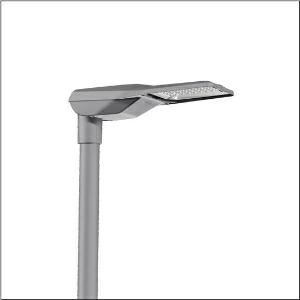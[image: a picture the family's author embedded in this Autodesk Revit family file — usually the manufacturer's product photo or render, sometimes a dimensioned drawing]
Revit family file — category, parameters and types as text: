
# Revit family: streetlight_sl_21_iq_mini___stw1_0a_5xe2e61d08hb_c7c8
name_source: partatom
category: Lighting Fixtures
units: mm (PartAtom-declared; Revit-internal decimal feet)

## family parameters
Cut with Voids When Loaded = No
Host = Face
Light Source = No
Part Type = Normal
Room Calculation Point = No
Round Connector Dimension = Use Diameter
Shared = No

## types (1)
- --- (1 x LED, 8480 lm, 70.9 W, 2700K)
    Apparent Load = 71 VA
    CIE Flux Codes = 38 75 98 100 100
    Color Rendering = 70
    Color Temperature = 2700K
    Default Elevation = 1800 mm
    Description = Streetlight SL 21 iQ mini, mast luminaire, primary light control with lens, of PMMA, primary optical cover: cover, of toughened safety glass, transparent, light distribution: STW1.0a, light emission: direct distribution, primary light characteristic: asymmetric, installation type: post-top, side-entry, LED, High Power LED, rated luminous flux: 8.480lm, luminous efficacy: 120lm/W, light colour: 727, colour temperature: 2700K, control: Auto-Match, Temp-Guard, Lumen-Switch, Night-Set, Smart-Wire, Light-Fading, Desk-Remote (wireless, voltage-free reading and setting of iQ features in the workshop via application-optimized NFC function/RFID function), optimised constant luminous flux control (CLO 2.0), presetting dimming linear, mains connection: 220..240V, AC, 50/60Hz, start of lifetime: 71W, end of service life: 75W, reduction: 31W, luminaire housing, of diecast aluminium, powder-coated, Siteco® metallic grey (DB 702S), corrosivity category C5 mid according to DIN EN ISO 12944, please order mast flange separately, inclination adjustable: 0°, 5°, 10°, 15°, sealing non-destructively replaceable, multi-level sealing system, length: 628mm, width: 235mm, height: 110mm, mast flange for spigot size: 42mm (side-entry): 5XC10008XM4, 60/48mm (side-entry/post-top): 5XC10108XM2, 76/60mm (side-entry/post-top): 5XC10108XM1, protection rating (complete): IP66, insulation class (complete): insulation class II (safety insulation), certification: CE, ENEC, ENEC+, VDE, impact resistance: IK09, permissible operating ambient temperature for outdoor applications: -40..+50°C, standard-compliant lighting for roads and squares, packaging unit: 1 piece

Light Distribution: STW1.0a
    Height = 110 mm
    Lamp = 1 x LED
    Lamp Light Flux = 8480 lm
    Lamp Power = 70.9 W
    Lamp count = 1
    Length = 625 mm
    Luminous efficacy = 120 lm/W
    Manufacturer = Siteco
    ModVariant = No
    Model = 5XE2E61D08HB
    Number of Poles = 1
    OnlyDefault = Yes
    Power Factor = 1
    Product Name = Streetlight SL 21 iQ mini | STW1.0a
    Product group = mast luminaire | pylon top
    ProductGroupID = 6100
    Protection Class = Protection class II
    Protection Degree = IP 66
    RLX_Detail_Level = 1
    RLX_Emergency_Light_Flux = 0 lm
    RLX_Emergency_Type = 0
    RLX_Emergency_Type_DB = No
    RlxData = <blob elided: 92381 chars, md5=722fe37a>
    Socket = socket
    Standby Power = 0 W
    System Light Flux = 8480 lm
    System Power = 71 W
    Type Comments = factory setting: luminous flux: 100 % | dim-lin: 254 | 711 mA
    Type Image = l_1003519.jpg
    URL = http://relux.com
    VarID = @adj_090267
    Voltage = 0 V
    Weight = 0.00 kg
    Width = 234 mm

## geometry (parser evidence)
native form markers: Blend x4, Sweep x10
no freeform markers — native parametric forms only
